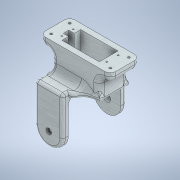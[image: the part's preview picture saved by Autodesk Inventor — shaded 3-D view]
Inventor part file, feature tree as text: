
AUTODESK INVENTOR PART (.ipt)
format: ipt  version: 2021 (Build 250183000, 183)  size: 746,496 bytes
history: native  units: mm
features: sketch x10, extrude x9, fillet x6, projected_geometry x2, plane x1
ambient origin geometry x8: Origin, YZ Plane, XZ Plane, XY Plane, X Axis, Y Axis, Z Axis, Center Point
bodies: Solid1 (feature_tree)
feature tree (28):
  extrude  "Extrusion1"  Depth=30.0mm
  extrude  "Extrusion2"  Depth=2.5mm TaperAngle=0.0deg
  plane  "Work Plane1"
  extrude  "Extrusion3"  Depth=3.5mm TaperAngle=0.0deg
  sketch  "Sketch4"  dims[d8=57.0mm d9=7.8mm d10=6.0mm d11=0.0mm]
  extrude  "Extrusion4"  Depth=7.8mm
  fillet  "Fillet1"  Radius=6.0mm
  extrude  "Extrusion5"  Depth=6.0mm
  extrude  "Extrusion6"  Depth=20.0mm
  extrude  "Extrusion7"  Depth=27.0mm TaperAngle=0.0deg
  fillet  "Fillet2"  Radius=27.0mm
  fillet  "Fillet3"  Radius=6.0mm
  fillet  "Fillet9"  Radius=7.0mm
  fillet  "Fillet7"  Radius=12.0mm
  extrude  "Extrusion8"  Depth=10.0mm
  fillet  "Fillet8"  Radius=10.0mm
  extrude  "Extrusion9"  Depth=27.0mm
  sketch  "Sketch1"  dims[d0=20.6mm d1=30.0mm]
  sketch  "Sketch2"  dims[d2=35.0mm d3=2.5mm d4=0.0mm]
  projected_geometry  "Projected Loop1"
  sketch  "Sketch3"  dims[d5=6.0mm d6=3.5mm d7=0.0mm]
  projected_geometry  "Projected Loop2"
  sketch  "Sketch5"  dims[d12=6.0mm d13=0.0mm d14=6.0mm]
  sketch  "Sketch6"  dims[d15=40.0mm d16=20.0mm]
  sketch  "Sketch7"  dims[d19=6.0mm d20=27.0mm d21=0.0mm d22=27.0mm d23=0.0mm d24=6.0mm d25=7.0mm d26=12.0mm]
  sketch  "Sketch8"  dims[d27=10.0mm d28=12.0mm d29=10.0mm]
  sketch  "Sketch9"  dims[d30=27.0mm d31=0.0mm d32=6.0mm]
  sketch  "Sketch10"  dims[d33=6.0mm d37=6.0mm d38=2.4mm d39=2.4mm d40=2.4mm d41=2.4mm d42=12.0mm d43=0.0mm d44=8.0mm d45=10.0mm d46=0.0mm d47=0.15mm d48=10.0mm d49=10.0mm d50=3.0mm d51=0.0mm]
